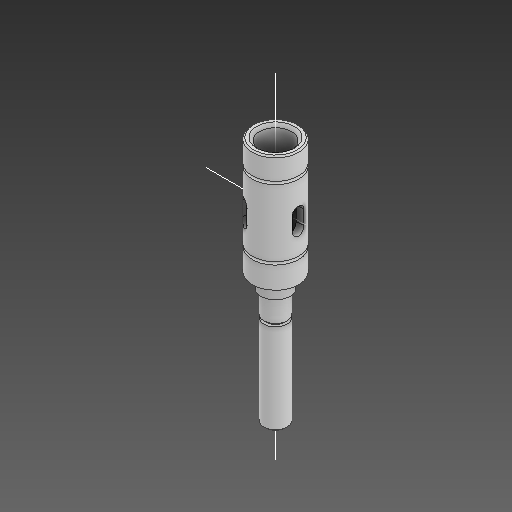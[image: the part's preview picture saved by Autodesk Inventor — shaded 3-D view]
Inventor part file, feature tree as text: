
AUTODESK INVENTOR PART (.ipt)
format: ipt  version: 2021 (Build 250183000, 183)  size: 218,624 bytes
history: native  units: in
note: dims shown in document units (in); Inventor stores cm internally (conversion verified against a paired STEP export)
features: sketch x9, other x8, plane x3
ambient origin geometry x8: Origin, YZ Plane, XZ Plane, XY Plane, X Axis, Y Axis, Z Axis, Center Point
bodies: Solid1 (feature_tree)
feature tree (20):
  other  "iner_sleeve.ipt"
  other  "Solid1::iner_sleeve.ipt"
  other  "TaggingFeature1"
  sketch  "Sketch1"  dims[d0=0.3937in]
  sketch  "Sketch2"
  sketch  "Sketch3"
  sketch  "Sketch5"
  sketch  "Sketch6"
  sketch  "Sketch7"
  sketch  "Sketch8"
  sketch  "Sketch10"
  sketch  "Sketch11"
  plane  "Work Plane1"
  plane  "Work Plane2"
  plane  "Work Plane3"
  other  "Work Axis1"
  other  "Work Axis2"
  other  "Work Axis3"
  other  "Srf1"
  other  "Srf1::Derived"
